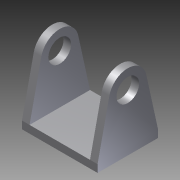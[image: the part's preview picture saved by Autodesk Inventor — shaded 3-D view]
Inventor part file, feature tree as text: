
AUTODESK INVENTOR PART (.ipt)
format: ipt  version: 2012 (Build 160160000, 160)  size: 110,080 bytes
history: native  units: in
note: dims shown in document units (in); Inventor stores cm internally (conversion verified against a paired STEP export)
features: extrude x2, sketch x2
ambient origin geometry x8: Origin, YZ Plane, XZ Plane, XY Plane, X Axis, Y Axis, Z Axis, Center Point
bodies: Solid1 (feature_tree)
feature tree (4):
  extrude  "Extrusion1"  Depth=1.25in
  extrude  "Extrusion2"  Depth=0.125in
  sketch  "Sketch1"  dims[d0=1.25in d1=1.25in]
  sketch  "Sketch2"  dims[d2=0.125in d3=0.125in d4=0.125in d5=1.0in d6=0.0in d7=0.625in d8=0.125in d9=0.375in d10=0.5in d11=1.0in d12=0.0in]
